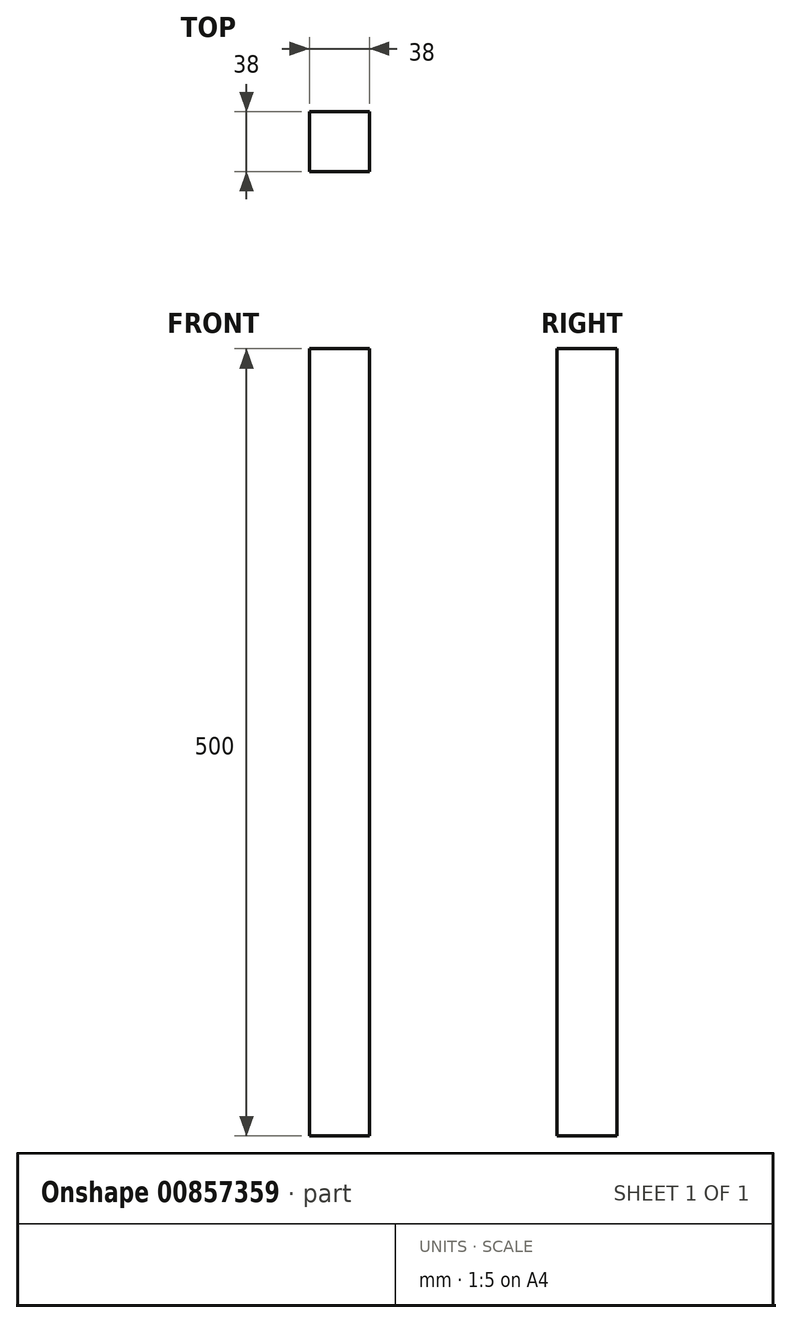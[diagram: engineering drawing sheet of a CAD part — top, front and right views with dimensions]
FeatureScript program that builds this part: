
annotation { "Feature Type Name" : "Feature", "Feature Type Description" : "" }
export const myFeature = defineFeature(function(context is Context, id is Id, definition is map)
    precondition{}
    {
        {
            var Q0;
            Q0=qCreatedBy(makeId("Top.planeOp"),FACE);
            var sketch = newSketch(context, id + "F0", { "sketchPlane" : qUnion([Q0])});
            skLineSegment(sketch, "E0.bottom", {"start": v(-21, 17) * mm, "end": v(17, 17) * mm});
            skLineSegment(sketch, "E0.top", {"start": v(-21, -21) * mm, "end": v(17, -21) * mm});
            skLineSegment(sketch, "E0.left", {"start": v(-21, 17) * mm, "end": v(-21, -21) * mm});
            skLineSegment(sketch, "E0.right", {"start": v(17, 17) * mm, "end": v(17, -21) * mm});
            skSolve(sketch);
        }
        {
            var Q0;
            Q0=makeQuery(id+"F0.imprint","IMPRINT",FACE,{"disambiguationData":[TD([[makeQuery(id+"F0.imprint","IMPRINT",EDGE,{"derivedFrom":sQuery(id+"F0.wireOp",EDGE,"E0.bottom")}),-1.0]])]});
            extrude(context, id + "F1", {"entities" : qUnion([Q0]), "depth" : 500 * mm, "offsetDistance" : 25 * mm});
        }
    });
